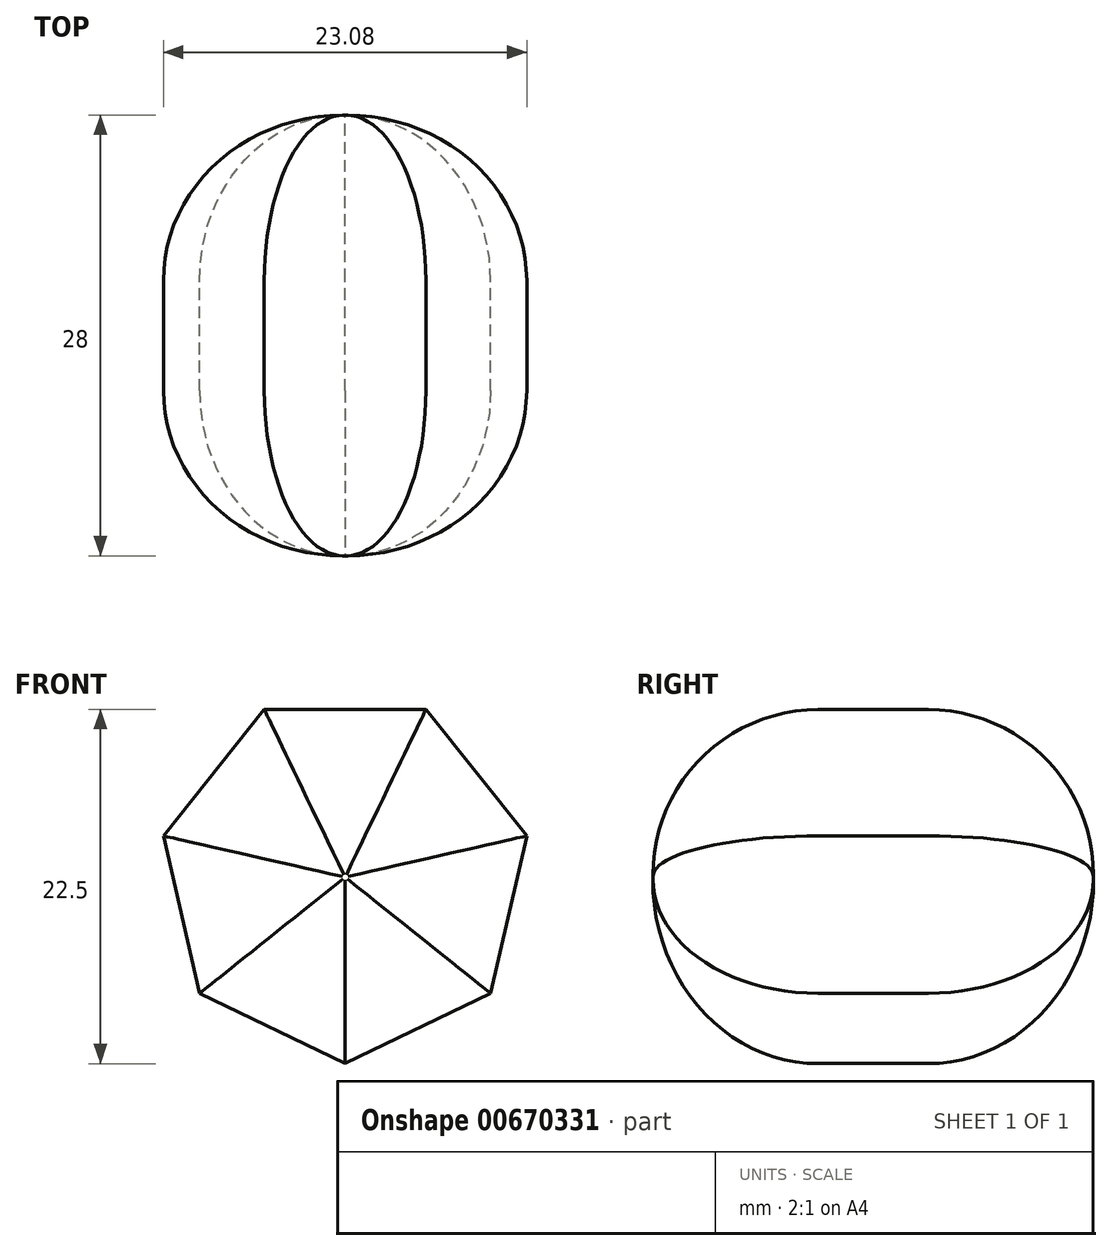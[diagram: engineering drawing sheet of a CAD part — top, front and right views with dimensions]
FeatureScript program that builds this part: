
annotation { "Feature Type Name" : "Feature", "Feature Type Description" : "" }
export const myFeature = defineFeature(function(context is Context, id is Id, definition is map)
    precondition{}
    {
        {
            var Q0;
            Q0=qCreatedBy(makeId("Front.planeOp"),FACE);
            var sketch = newSketch(context, id + "F0", { "sketchPlane" : qUnion([Q0])});
            skCircle(sketch, "E0.cCircle", {"center": v(0, 0) * mm, "radius": 10.66 * mm, "construction": true});
            skLineSegment(sketch, "E0.0", {"start": v(-5.14, 10.66) * mm, "end": v(5.14, 10.66) * mm});
            skLineSegment(sketch, "E0.1", {"start": v(5.14, 10.66) * mm, "end": v(11.54, 2.63) * mm});
            skLineSegment(sketch, "E0.2", {"start": v(11.54, 2.63) * mm, "end": v(9.25, -7.38) * mm});
            skLineSegment(sketch, "E0.3", {"start": v(9.25, -7.38) * mm, "end": v(0, -11.84) * mm});
            skLineSegment(sketch, "E0.4", {"start": v(0, -11.84) * mm, "end": v(-9.25, -7.38) * mm});
            skLineSegment(sketch, "E0.5", {"start": v(-9.25, -7.38) * mm, "end": v(-11.54, 2.63) * mm});
            skLineSegment(sketch, "E0.6", {"start": v(-11.54, 2.63) * mm, "end": v(-5.14, 10.66) * mm});
            skPoint(sketch, "E0.0.midPoint", {"position": v(0, 10.66) * mm});
            skSolve(sketch);
        }
        {
            var Q0;
            Q0 = qSketchRegion(id + "F0", true);
            extrude(context, id + "F1", {"entities" : qUnion([Q0]), "depth" : 14 * mm, "offsetDistance" : 25 * mm, "hasSecondDirection" : true, "secondDirectionOppositeDirection" : true, "secondDirectionDepth" : 14 * mm});
        }
        {
            var Q0;
            Q0=makeQuery(id+"F1.opExtrude","CAP_FACE",FACE,{"disambiguationData":[OSD([sQuery(id+"F0.wireOp",EDGE,"E0.0"),sQuery(id+"F0.wireOp",EDGE,"E0.1"),sQuery(id+"F0.wireOp",EDGE,"E0.2"),sQuery(id+"F0.wireOp",EDGE,"E0.3"),sQuery(id+"F0.wireOp",EDGE,"E0.4"),sQuery(id+"F0.wireOp",EDGE,"E0.5"),sQuery(id+"F0.wireOp",EDGE,"E0.6")])],"isStart":false});
            var Q1;
            Q1=makeQuery(id+"F1.opExtrude","CAP_FACE",FACE,{"disambiguationData":[OSD([sQuery(id+"F0.wireOp",EDGE,"E0.0"),sQuery(id+"F0.wireOp",EDGE,"E0.1"),sQuery(id+"F0.wireOp",EDGE,"E0.2"),sQuery(id+"F0.wireOp",EDGE,"E0.3"),sQuery(id+"F0.wireOp",EDGE,"E0.4"),sQuery(id+"F0.wireOp",EDGE,"E0.5"),sQuery(id+"F0.wireOp",EDGE,"E0.6")])],"isStart":true});
            fillet(context, id + "F2", {"entities" : qUnion([Q0, Q1]), "radius" : 10.5 * mm, "tangentPropagation" : true, "allowEdgeOverflow" : false});
        }
    });
